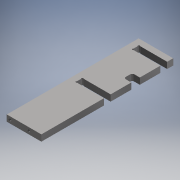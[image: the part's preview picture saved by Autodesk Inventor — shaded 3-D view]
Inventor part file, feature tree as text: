
AUTODESK INVENTOR PART (.ipt)
format: ipt  version: 2018 (Build 220112000, 112)  size: 157,184 bytes
history: native  units: mm
features: reference x6, extrude x2, hole x1, sketch x1
ambient origin geometry x8: Origin, YZ Plane, XZ Plane, XY Plane, X Axis, Y Axis, Z Axis, Center Point
bodies: Volumenkörper1 (feature_tree)
feature tree (10):
  extrude  "Extrusion1"  Depth=55.0mm
  extrude  "Extrusion2"  Depth=10.0mm TaperAngle=0.0deg
  hole  "Bohrung1"  [1 undecoded]
  sketch  "Skizze2"  dims[d0=210.0mm d1=55.0mm d2=10.0mm d3=0.0mm d4=0.3mm d5=0.3mm d6=3.0mm d7=3.0mm d8=0.8mm d9=0.8mm d10=0.8mm d11=0.8mm d13=10.6mm d14=45.0mm d15=0.3mm d16=0.3mm d17=12.1mm d18=3.0mm d19=10.0mm d20=0.0mm d21=30.0mm d22=5.0mm d23=5.0mm d24=5.0mm d25=4.134mm d26=12.0mm d27=4.0mm d28=2.0mm d29=90.0deg d30=15.0mm d31=20.594885mm]
  reference  "Referenz1"
  reference  "Referenz2"
  reference  "Referenz3"
  reference  "Referenz4"
  reference  "Referenz5"
  reference  "Referenz6"
note: 1 required parameter value undecoded (feature->parameter linkage not recoverable at this tier; creation-order binding heuristic only, values carry confidence <= 0.55)
